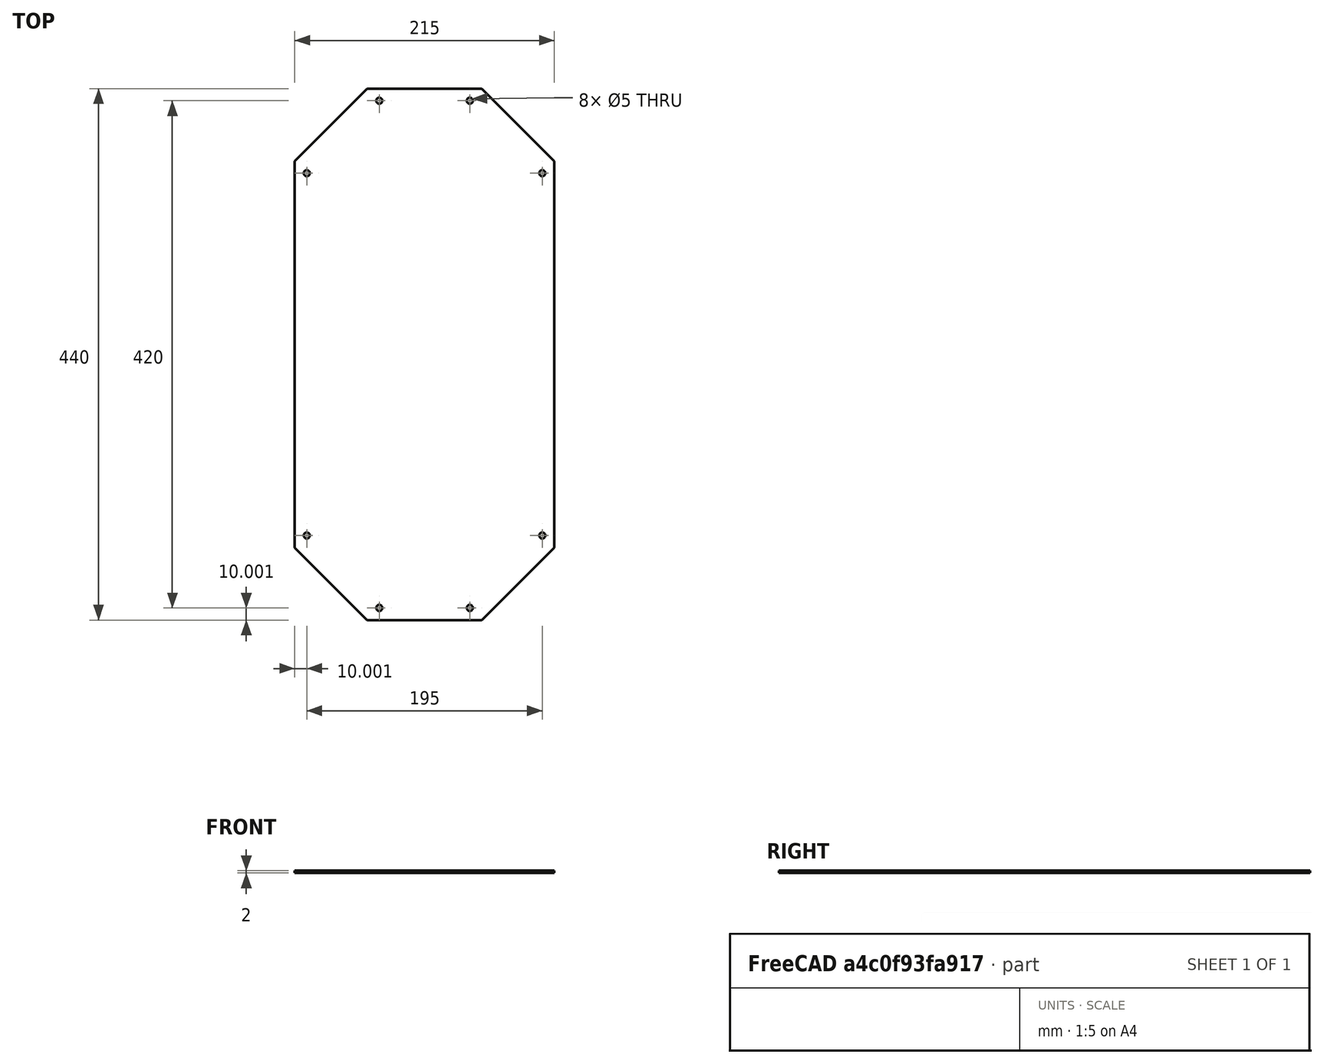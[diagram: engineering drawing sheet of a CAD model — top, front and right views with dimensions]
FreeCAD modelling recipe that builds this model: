
FCSTD DOCUMENT  (FreeCAD 0.16R6698 (Git))
Label: plaque sup equerre -
License: All rights reserved
LicenseURL: http://en.wikipedia.org/wiki/All_rights_reserved
objects: Sketcher::SketchObject×1, PartDesign::Pad×1
note: 3 computed .brp shape members not serialized (recipe doc carries the construction recipe); baked Part::Feature solids carry a one-line shape summary decoded from their .brp

FEATURE [Sketcher::SketchObject] Sketch
  sketch-geometry (16):
    g0: LineSegment StartX=-45.4586 StartY=215.82 StartZ=0 EndX=49.5414 EndY=215.82 EndZ=0
    g1: LineSegment StartX=109.541 StartY=155.82 StartZ=0 EndX=109.541 EndY=-164.18 EndZ=0
    g2: LineSegment StartX=49.5414 StartY=-224.18 StartZ=0 EndX=-45.4586 EndY=-224.18 EndZ=0
    g3: LineSegment StartX=-105.459 StartY=-164.18 StartZ=0 EndX=-105.459 EndY=155.82 EndZ=0
    g4: LineSegment StartX=-45.4586 StartY=215.82 StartZ=0 EndX=-105.459 EndY=155.82 EndZ=0
    g5: LineSegment StartX=49.5414 StartY=215.82 StartZ=0 EndX=109.541 EndY=155.82 EndZ=0
    g6: LineSegment StartX=109.541 StartY=-164.18 StartZ=0 EndX=49.5414 EndY=-224.18 EndZ=0
    g7: LineSegment StartX=-105.459 StartY=-164.18 StartZ=0 EndX=-45.4586 EndY=-224.18 EndZ=0
    g8: Circle CenterX=-95.4586 CenterY=145.82 CenterZ=0 NormalX=0 NormalY=0 NormalZ=1 Radius=2.5
    g9: Circle CenterX=-35.4586 CenterY=205.82 CenterZ=0 NormalX=0 NormalY=0 NormalZ=1 Radius=2.5
    g10: Circle CenterX=39.5414 CenterY=205.82 CenterZ=0 NormalX=0 NormalY=0 NormalZ=1 Radius=2.5
    g11: Circle CenterX=99.5414 CenterY=145.82 CenterZ=0 NormalX=0 NormalY=0 NormalZ=1 Radius=2.5
    g12: Circle CenterX=-95.4586 CenterY=-154.18 CenterZ=0 NormalX=0 NormalY=0 NormalZ=1 Radius=2.5
    g13: Circle CenterX=-35.4586 CenterY=-214.18 CenterZ=0 NormalX=0 NormalY=0 NormalZ=1 Radius=2.5
    g14: Circle CenterX=39.5414 CenterY=-214.18 CenterZ=0 NormalX=0 NormalY=0 NormalZ=1 Radius=2.5
    g15: Circle CenterX=99.5414 CenterY=-154.18 CenterZ=0 NormalX=0 NormalY=0 NormalZ=1 Radius=2.5
  constraints (46):
    c: Horizontal(g0)
    c: Horizontal(g2)
    c: Vertical(g1)
    c: Vertical(g3)
    c: Coincident(g4,g0)
    c: Coincident(g4,g3)
    c: Coincident(g5,g0)
    c: Coincident(g5,g1)
    c: Coincident(g6,g2)
    c: Coincident(g6,g1)
    c: Coincident(g7,g3)
    c: Coincident(g7,g2)
    c: DistanceX(g7,g7) = 60
    c: DistanceY(g7,g7) = 60
    c: DistanceX(g6,g6) = 60
    c: DistanceY(g6,g6) = 60
    c: DistanceX(g4,g4) = 60
    c: DistanceY(g5,g5) = 60
    c: DistanceY(g4,g4) = 60
    c: DistanceX(g5,g5) = 60
    c: DistanceX(g0,g0) = 95
    c: DistanceY(g3,g3) = 320
    c: Radius(g11) = 2.5
    c: Radius(g10) = 2.5
    c: Radius(g9) = 2.5
    c: Radius(g8) = 2.5
    c: DistanceX(g3,g8) = 10
    c: DistanceY(g8,g3) = 10
    c: DistanceX(g0,g9) = 10
    c: DistanceY(g9,g0) = 10
    c: DistanceX(g10,g0) = 10
    c: DistanceY(g10,g0) = 10
    c: DistanceX(g11,g1) = 10
    c: DistanceY(g11,g1) = 10
    c: Radius(g15) = 2.5
    c: Equal(g15,g14)
    c: Equal(g15,g13)
    c: Equal(g15,g12)
    c: DistanceX(g3,g12) = 10
    c: DistanceY(g3,g12) = 10
    c: DistanceX(g2,g13) = 10
    c: DistanceY(g2,g13) = 10
    c: DistanceY(g2,g14) = 10
    c: DistanceX(g14,g2) = 10
    c: DistanceY(g1,g15) = 10
    c: DistanceX(g15,g1) = 10
FEATURE [PartDesign::Pad] Pad
  Length = 2
  Length2 = 100
  Sketch = -> Sketch
  Type = 0
